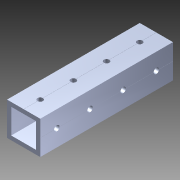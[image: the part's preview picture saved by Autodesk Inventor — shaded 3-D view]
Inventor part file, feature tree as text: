
AUTODESK INVENTOR PART (.ipt)
format: ipt  version: 2014 SP1 (Build 180222100, 222)  size: 1,117,184 bytes
history: native  units: in
note: dims shown in document units (in); Inventor stores cm internally (conversion verified against a paired STEP export)
features: pattern_circular x1, other x1, plane x1, extrude x1, imported_body x1, sketch x1
ambient origin geometry x8: Origin, YZ Plane, XZ Plane, XY Plane, X Axis, Y Axis, Z Axis, Center Point
bodies: Body1 (feature_tree)
feature tree (6):
  pattern_circular  "CirPattern2"
  other  "217-3426-STEP1"
  plane  "Work Plane1"
  extrude  "Extrusion1"  Depth=3937.0079in TaperAngle=0.0deg
  imported_body  "Base1"
  sketch  "Sketch1"  dims[d0=-4.0in d1=3937.0079in d2=0.0in]
